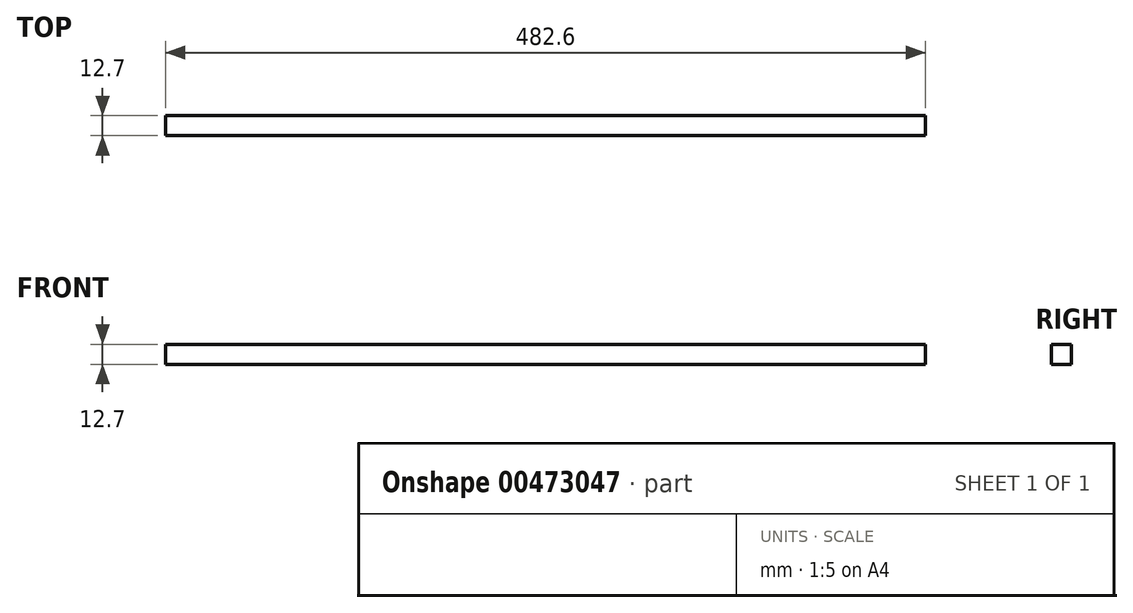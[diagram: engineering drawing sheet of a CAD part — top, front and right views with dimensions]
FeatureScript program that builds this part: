
annotation { "Feature Type Name" : "Feature", "Feature Type Description" : "" }
export const myFeature = defineFeature(function(context is Context, id is Id, definition is map)
    precondition{}
    {
        {
            var Q0;
            Q0=qCreatedBy(makeId("Top.planeOp"),FACE);
            var sketch = newSketch(context, id + "F0", { "sketchPlane" : qUnion([Q0])});
            skLineSegment(sketch, "E0.bottom", {"start": v(241.3, 6.35) * mm, "end": v(-241.3, 6.35) * mm});
            skLineSegment(sketch, "E0.top", {"start": v(241.3, -6.35) * mm, "end": v(-241.3, -6.35) * mm});
            skLineSegment(sketch, "E0.left", {"start": v(241.3, 6.35) * mm, "end": v(241.3, -6.35) * mm});
            skLineSegment(sketch, "E0.right", {"start": v(-241.3, 6.35) * mm, "end": v(-241.3, -6.35) * mm});
            skPoint(sketch, "E0.middle", {"position": v(0, 0) * mm});
            skSolve(sketch);
        }
        {
            var Q0;
            Q0=makeQuery(id+"F0.imprint","IMPRINT",FACE,{"disambiguationData":[TD([[makeQuery(id+"F0.imprint","IMPRINT",EDGE,{"derivedFrom":sQuery(id+"F0.wireOp",EDGE,"E0.bottom")}),1.0]])]});
            extrude(context, id + "F1", {"entities" : qUnion([Q0]), "depth" : 12.7 * mm});
        }
    });
